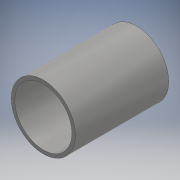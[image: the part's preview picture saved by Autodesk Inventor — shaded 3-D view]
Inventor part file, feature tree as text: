
AUTODESK INVENTOR PART (.ipt)
format: ipt  version: 2018.1 (Build 221171000, 171)  size: 113,664 bytes
history: native  units: mm
features: extrude x1, sketch x1
ambient origin geometry x8: Origin, YZ Plane, XZ Plane, XY Plane, X Axis, Y Axis, Z Axis, Center Point
bodies: Body1 (feature_tree)
feature tree (2):
  extrude  "押し出し1"  Depth=5.5mm
  sketch  "スケッチ1"
